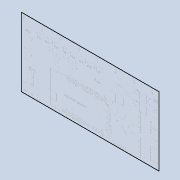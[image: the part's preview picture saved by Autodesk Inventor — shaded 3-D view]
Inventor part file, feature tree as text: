
AUTODESK INVENTOR PART (.ipt)
format: ipt  version: 2022 (Build 260153000, 153)  size: 891,392 bytes
history: native  units: in
note: dims shown in document units (in); Inventor stores cm internally (conversion verified against a paired STEP export)
features: sketch x1, extrude x1, other x1
ambient origin geometry x8: Origin, YZ Plane, XZ Plane, XY Plane, X Axis, Y Axis, Z Axis, Center Point
bodies: Solid1 (feature_tree)
feature tree (3):
  sketch  "Sketch1"  dims[d1=9.0in d5=0.01in d6=0.0in]
  extrude  "Extrusion1"  Depth=0.01in TaperAngle=0.0deg
  other  "Image1"
